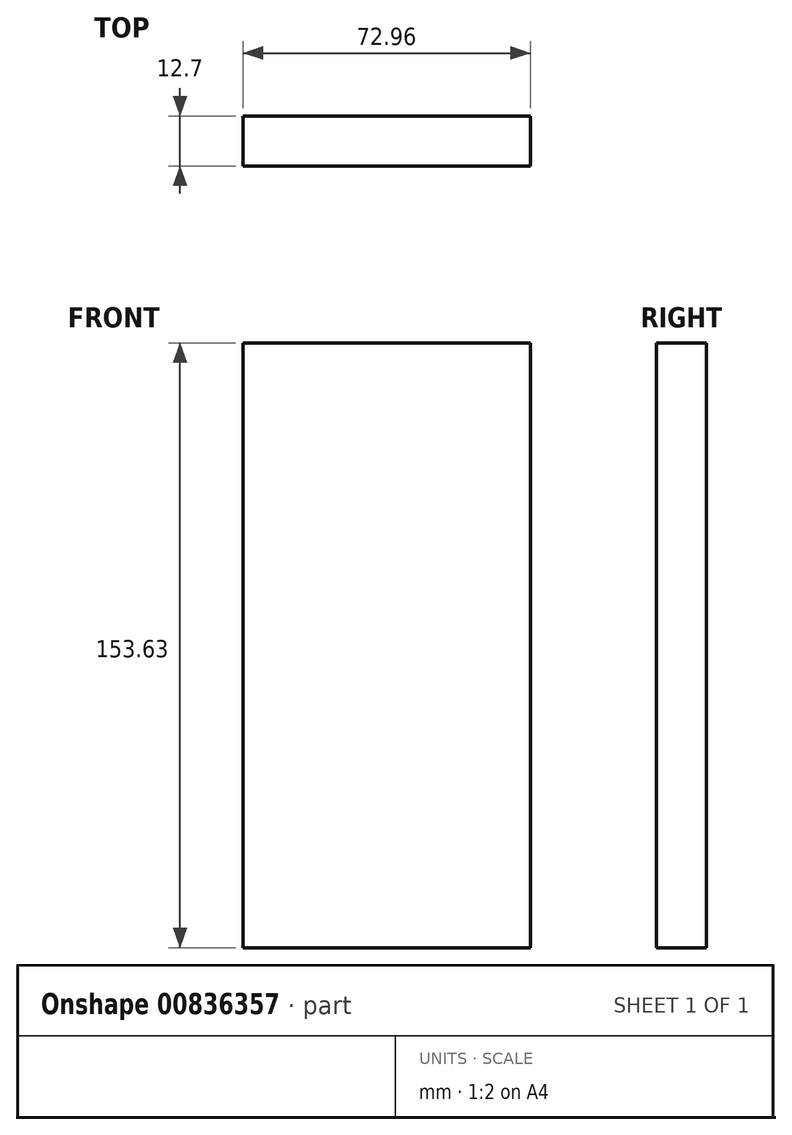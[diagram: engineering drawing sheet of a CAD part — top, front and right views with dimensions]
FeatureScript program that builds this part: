
annotation { "Feature Type Name" : "Feature", "Feature Type Description" : "" }
export const myFeature = defineFeature(function(context is Context, id is Id, definition is map)
    precondition{}
    {
        {
            var Q0;
            Q0=qCreatedBy(makeId("Front.planeOp"),FACE);
            var sketch = newSketch(context, id + "F0", { "sketchPlane" : qUnion([Q0])});
            skLineSegment(sketch, "E0.bottom", {"start": v(43.63, 75.4) * mm, "end": v(-29.33, 75.4) * mm});
            skLineSegment(sketch, "E0.top", {"start": v(43.63, -78.23) * mm, "end": v(-29.33, -78.23) * mm});
            skLineSegment(sketch, "E0.left", {"start": v(43.63, 75.4) * mm, "end": v(43.63, -78.23) * mm});
            skLineSegment(sketch, "E0.right", {"start": v(-29.33, 75.4) * mm, "end": v(-29.33, -78.23) * mm});
            skSolve(sketch);
        }
        {
            var Q0;
            Q0=makeQuery(id+"F0.imprint","IMPRINT",FACE,{"disambiguationData":[TD([[makeQuery(id+"F0.imprint","IMPRINT",EDGE,{"derivedFrom":sQuery(id+"F0.wireOp",EDGE,"E0.bottom")}),1.0]])]});
            extrude(context, id + "F1", {"entities" : qUnion([Q0]), "oppositeDirection" : true, "depth" : 12.7 * mm, "offsetDistance" : 25.4 * mm});
        }
    });
